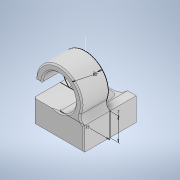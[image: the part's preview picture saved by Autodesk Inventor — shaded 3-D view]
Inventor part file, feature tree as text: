
AUTODESK INVENTOR PART (.ipt)
format: ipt  version: 2021 (Build 250183000, 183)  size: 461,312 bytes
history: native  units: mm
features: extrude x4, sketch x3, fillet x3, chamfer x2, other x1
ambient origin geometry x8: Origin, YZ Plane, XZ Plane, XY Plane, X Axis, Y Axis, Z Axis, Center Point
bodies: Solid1 (feature_tree)
feature tree (13):
  sketch  "Sketch1"  dims[d0=10.0mm d1=2.0mm]
  extrude  "Extrusion1"  Depth=10.0mm
  extrude  "Extrusion2"  Depth=15.0mm
  other  "Work Point1"
  extrude  "Extrusion3"  Depth=0.4mm TaperAngle=0.0deg
  chamfer  "Chamfer1"  Distance=3.2mm
  fillet  "Fillet1"  Radius=10.0mm
  fillet  "Fillet2"  Radius=2.0mm
  chamfer  "Chamfer2"  Distance=2.0mm
  extrude  "Extrusion4"  Depth=0.4mm
  fillet  "Fillet3"  Radius=0.4mm
  sketch  "Sketch2"  dims[d2=7.0mm d3=15.0mm]
  sketch  "Sketch3"  dims[d4=8.0mm d5=0.0mm d6=8.0mm d7=0.0mm d8=3.2mm d9=10.0mm d10=0.0mm d11=2.0mm d12=2.0mm d13=45.0deg d14=2.0mm d15=0.4mm d16=0.4mm d17=2.0mm d18=45.0deg d19=5.0mm d20=0.0mm d21=0.0mm d22=0.4mm]
